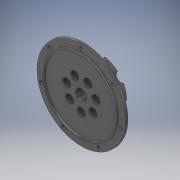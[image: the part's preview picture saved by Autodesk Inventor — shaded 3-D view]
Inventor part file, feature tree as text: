
AUTODESK INVENTOR PART (.ipt)
format: ipt  version: 2018 (Build 220112000, 112)  size: 835,584 bytes
history: native  units: mm
features: sketch x10, extrude x7, thread x7, fillet x2, plane x2, revolve x1, sweep x1, other x1, pattern_circular x1, chamfer x1
ambient origin geometry x8: Origin, YZ Plane, XZ Plane, XY Plane, X Axis, Y Axis, Z Axis, Center Point
bodies: Solid1 (feature_tree)
feature tree (33):
  revolve  "Revolution1"  [1 undecoded]
  extrude  "Extrusion1"  Depth=40.25mm
  fillet  "Fillet1"  Radius=50.0mm
  extrude  "Extrusion2"  Depth=5.0mm
  plane  "Work Plane1"
  extrude  "Extrusion3"  Depth=0.75mm
  extrude  "Extrusion4"  TaperAngle=90.0deg  [1 undecoded]
  sweep  "Sweep1"
  fillet  "Fillet2"  Radius=10.0mm
  plane  "Work Plane2"
  extrude  "Extrusion5"  Depth=1.0mm
  extrude  "Extrusion6"  Depth=9.5mm
  other  "Work Axis1"
  pattern_circular  "Circular Pattern1"  [2 undecoded]
  extrude  "Extrusion7"  Depth=10.0mm TaperAngle=0.0deg
  thread  "Thread1"  [1 undecoded]
  thread  "Thread2"  [1 undecoded]
  thread  "Thread3"  [1 undecoded]
  thread  "Thread4"  [1 undecoded]
  thread  "Thread5"  [1 undecoded]
  thread  "Thread6"  [1 undecoded]
  thread  "Thread7"  [1 undecoded]
  chamfer  "Chamfer1"  Distance=3.0mm
  sketch  "Sketch1"  dims[d0=6.5mm d1=22.0mm]
  sketch  "Sketch2"  dims[d2=40.25mm d3=42.375mm d4=50.0mm]
  sketch  "Sketch3"  dims[d5=3.0mm d6=5.0mm]
  sketch  "Sketch4"  dims[d8=30.0mm d11=0.75mm]
  sketch  "Sketch5"  dims[d12=1.4mm d13=90.0deg]
  sketch  "Sketch6"  dims[d14=10.0mm d15=70.0mm d17=360.0deg d19=10.0mm d20=0.0mm]
  sketch  "Sketch7"  dims[d21=1.0mm d22=2.5mm]
  sketch  "Sketch8"  dims[d23=9.5mm d24=9.5mm]
  sketch  "Sketch9"  dims[d25=50.5mm d26=0.0mm]
  sketch  "Sketch10"  dims[d27=25.0mm d28=5.0mm d29=2.8mm d30=1.4mm d31=0.0mm d32=0.0mm d33=9.0mm d34=17.0mm d35=7.0mm d36=4.2mm d37=0.0mm d38=1.7mm d39=3.5mm d40=3.5mm d41=3.0mm d42=0.0mm d43=0.0mm d44=2.0mm d45=-30.0mm d46=12.15mm d47=2.0mm d48=0.0mm d49=10.42mm d50=5.0mm d51=0.0mm d52=70.0mm d53=360.0deg d55=4.0mm d56=46.0mm d57=70.0mm d59=360.0deg d61=5.0mm d62=0.0mm d63=10.0mm d64=0.0mm d65=10.0mm d66=0.0mm d67=10.0mm d68=0.0mm d69=10.0mm d70=0.0mm d71=10.0mm d72=0.0mm d73=10.0mm d74=0.0mm d75=10.0mm d76=0.0mm d77=0.5mm d78=2.0mm d79=45.0deg d81=9.5mm]
note: 11 required parameter values undecoded (feature->parameter linkage not recoverable at this tier; creation-order binding heuristic only, values carry confidence <= 0.55)